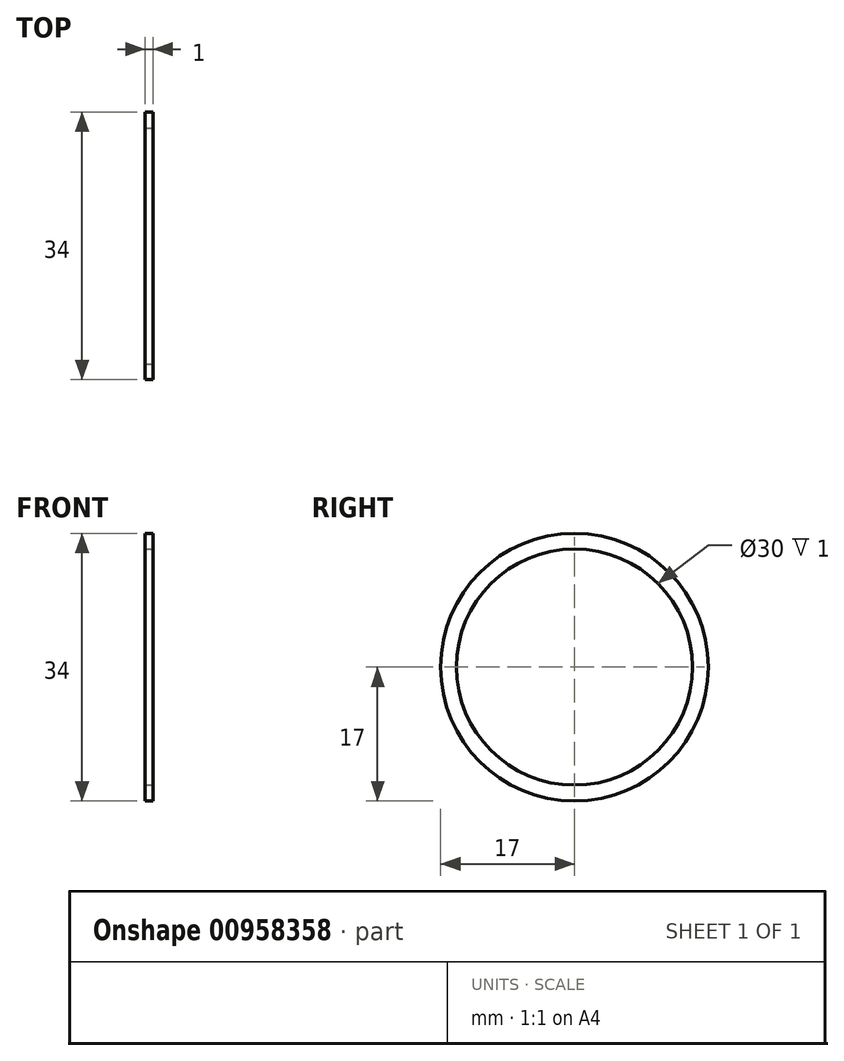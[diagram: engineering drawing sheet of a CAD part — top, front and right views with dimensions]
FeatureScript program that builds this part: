
annotation { "Feature Type Name" : "Feature", "Feature Type Description" : "" }
export const myFeature = defineFeature(function(context is Context, id is Id, definition is map)
    precondition{}
    {
        {
            var Q0;
            Q0=qCreatedBy(makeId("Front.planeOp"),FACE);
            var sketch = newSketch(context, id + "F0", { "sketchPlane" : qUnion([Q0])});
            skLineSegment(sketch, "E0.bottom", {"start": v(-14.02, 17) * mm, "end": v(-15.02, 17) * mm});
            skLineSegment(sketch, "E0.top", {"start": v(-14.02, 15) * mm, "end": v(-15.02, 15) * mm});
            skLineSegment(sketch, "E0.left", {"start": v(-14.02, 17) * mm, "end": v(-14.02, 15) * mm});
            skLineSegment(sketch, "E0.right", {"start": v(-15.02, 17) * mm, "end": v(-15.02, 15) * mm});
            skLineSegment(sketch, "E1", {"start": v(0, 0) * mm, "end": v(-14.12, 0) * mm});
            skSolve(sketch);
        }
        {
            var Q0;
            Q0=qSketchRegion(id+"F0",true);
            var Q1;
            Q1=sQuery(id+"F0.wireOp",EDGE,"E1");
            revolve(context, id + "F1", {"surfaceOperationType" : NewSurfaceOperationType.NEW, "entities" : qUnion([Q0]), "axis" : qUnion([Q1]), "revolveType" : RevolveType.FULL});
        }
    });
